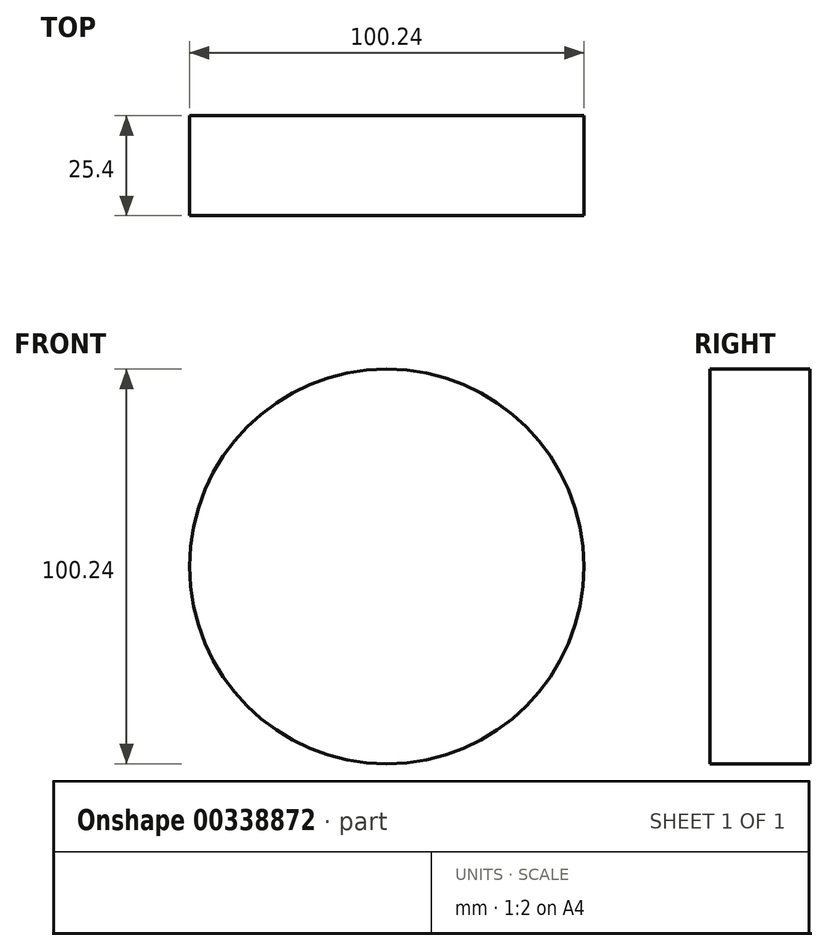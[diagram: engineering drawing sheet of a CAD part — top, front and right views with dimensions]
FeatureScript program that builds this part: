
annotation { "Feature Type Name" : "Feature", "Feature Type Description" : "" }
export const myFeature = defineFeature(function(context is Context, id is Id, definition is map)
    precondition{}
    {
        {
            var Q0;
            Q0=qCreatedBy(makeId("Front.planeOp"),FACE);
            var sketch = newSketch(context, id + "F0", { "sketchPlane" : qUnion([Q0])});
            skCircle(sketch, "E0", {"center": v(0, 0) * mm, "radius": 50.12 * mm});
            skSolve(sketch);
        }
        {
            var Q0;
            Q0=makeQuery(id+"F0.imprint","IMPRINT",FACE,{"disambiguationData":[TD([[makeQuery(id+"F0.imprint","IMPRINT",EDGE,{"derivedFrom":sQuery(id+"F0.wireOp",EDGE,"E0")}),1.0]])]});
            extrude(context, id + "F1", {"entities" : qUnion([Q0]), "depth" : 25.4 * mm});
        }
    });
